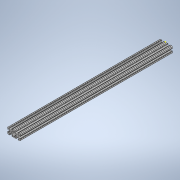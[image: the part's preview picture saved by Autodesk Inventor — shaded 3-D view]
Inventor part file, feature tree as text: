
AUTODESK INVENTOR PART (.ipt)
format: ipt  version: 2020 (Build 240168000, 168)  size: 334,336 bytes
history: native  units: in
note: dims shown in document units (in); Inventor stores cm internally (conversion verified against a paired STEP export)
features: sketch x2, extrude x1
ambient origin geometry x8: Origin, YZ Plane, XZ Plane, XY Plane, X Axis, Y Axis, Z Axis, Center Point
bodies: Solid1 (feature_tree)
feature tree (3):
  extrude  "Extrusion1"  [1 undecoded]
  sketch  "Sketch2"
  sketch  "Sketch1"  dims[d0=24.0in d1=0.0in]
note: 1 required parameter value undecoded (feature->parameter linkage not recoverable at this tier; creation-order binding heuristic only, values carry confidence <= 0.55)
